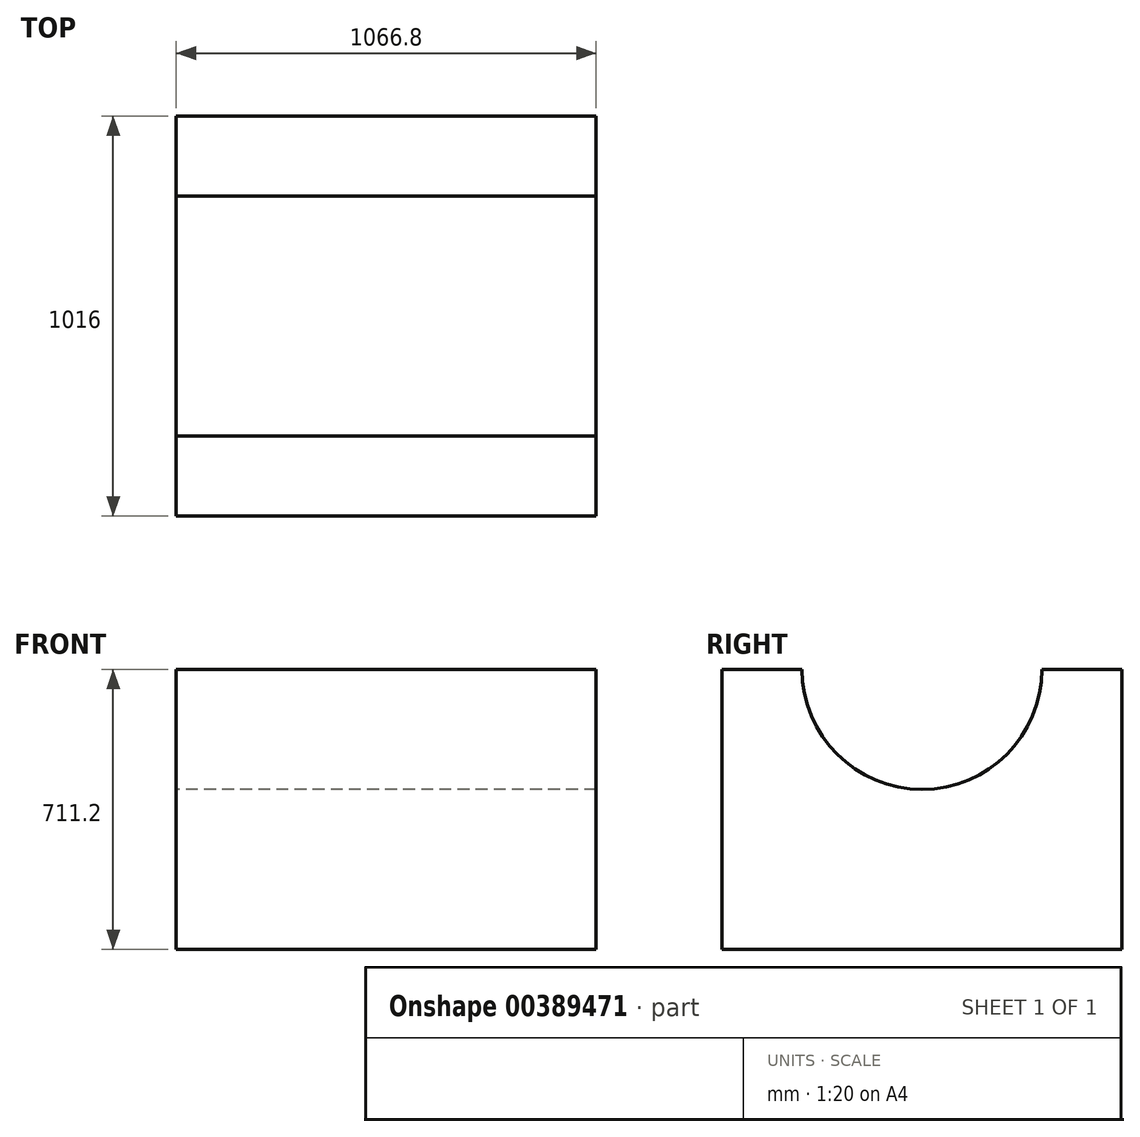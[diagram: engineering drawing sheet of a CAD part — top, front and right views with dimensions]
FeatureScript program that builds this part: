
annotation { "Feature Type Name" : "Feature", "Feature Type Description" : "" }
export const myFeature = defineFeature(function(context is Context, id is Id, definition is map)
    precondition{}
    {
        {
            var Q0;
            Q0=qCreatedBy(makeId("Right.planeOp"),FACE);
            var sketch = newSketch(context, id + "F0", { "sketchPlane" : qUnion([Q0])});
            skLineSegment(sketch, "E0", {"start": v(0, 0) * mm, "end": v(-1016, 0) * mm});
            skLineSegment(sketch, "E1", {"start": v(-1016, 0) * mm, "end": v(-1016, 711.2) * mm});
            skLineSegment(sketch, "E2", {"start": v(-1016, 711.2) * mm, "end": v(-812.8, 711.2) * mm});
            skLineSegment(sketch, "E3", {"start": v(0, 711.2) * mm, "end": v(0, 0) * mm});
            skArc(sketch, "E4", {"start": v(-812.8, 711.2) * mm, "mid": v(-508, 406.4) * mm, "end": v(-203.2, 711.2) * mm});
            skLineSegment(sketch, "E5.trimOffspring", {"start": v(-203.2, 711.2) * mm, "end": v(0, 711.2) * mm});
            skSolve(sketch);
        }
        {
            var Q0;
            Q0=makeQuery(id+"F0.imprint","IMPRINT",FACE,{"disambiguationData":[TD([[makeQuery(id+"F0.imprint","IMPRINT",EDGE,{"derivedFrom":sQuery(id+"F0.wireOp",EDGE,"E0")}),-1.0]])]});
            extrude(context, id + "F1", {"entities" : qUnion([Q0]), "depth" : 1066.8 * mm});
        }
    });
